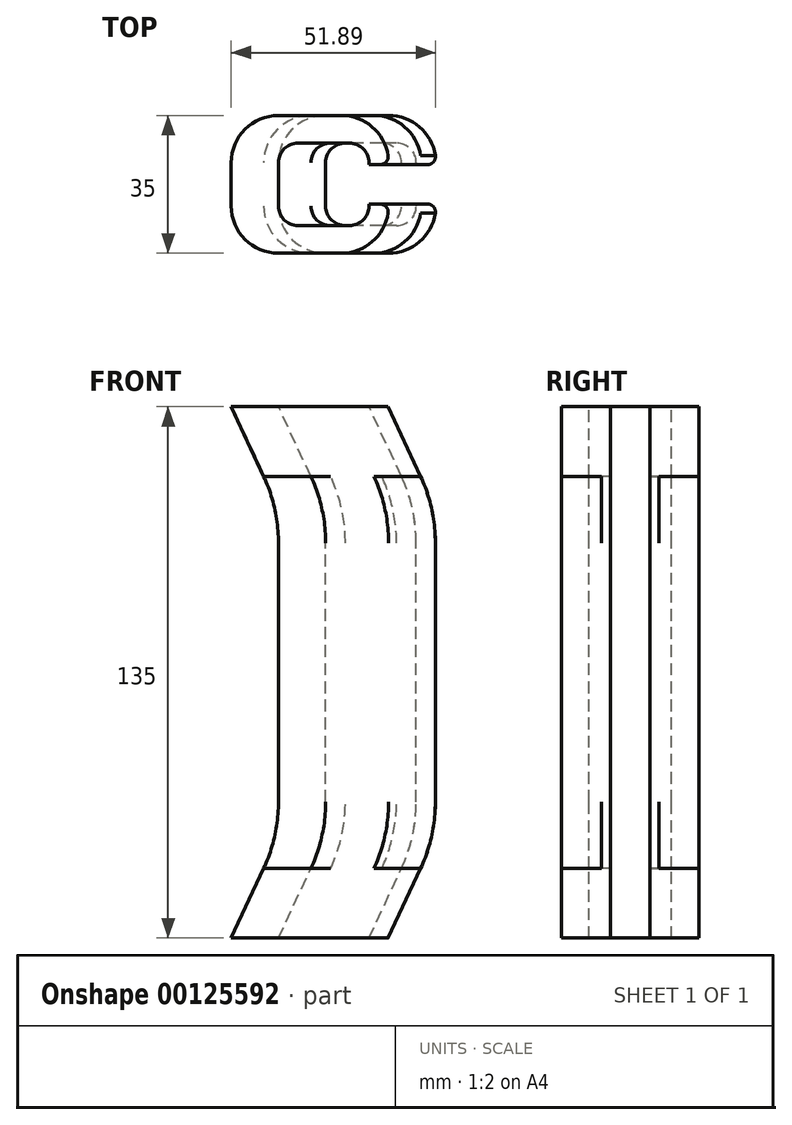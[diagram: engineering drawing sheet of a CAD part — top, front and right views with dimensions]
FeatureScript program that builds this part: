
annotation { "Feature Type Name" : "Feature", "Feature Type Description" : "" }
export const myFeature = defineFeature(function(context is Context, id is Id, definition is map)
    precondition{}
    {
        {
            var Q0;
            Q0=qCreatedBy(makeId("Top.planeOp"),FACE);
            var sketch = newSketch(context, id + "F0", { "sketchPlane" : qUnion([Q0])});
            skLineSegment(sketch, "E0.bottom", {"start": v(0, 17.5) * mm, "end": v(16, 17.5) * mm});
            skLineSegment(sketch, "E0.top", {"start": v(0, -17.5) * mm, "end": v(16, -17.5) * mm});
            skLineSegment(sketch, "E0.left", {"start": v(-12, 5.5) * mm, "end": v(-12, -5.5) * mm});
            skLineSegment(sketch, "E0.right", {"start": v(28, 5.5) * mm, "end": v(28, 5) * mm});
            skLineSegment(sketch, "E1.bottom", {"start": v(5, 10.5) * mm, "end": v(18, 10.5) * mm});
            skLineSegment(sketch, "E1.top", {"start": v(5, -10.5) * mm, "end": v(18, -10.5) * mm});
            skLineSegment(sketch, "E1.left", {"start": v(0, 5.5) * mm, "end": v(0, -5.5) * mm});
            skLineSegment(sketch, "E1.right", {"start": v(23, 5.5) * mm, "end": v(23, 5) * mm});
            skLineSegment(sketch, "E2.bottom", {"start": v(23, -5) * mm, "end": v(28, -5) * mm});
            skLineSegment(sketch, "E2.top", {"start": v(23, 5) * mm, "end": v(28, 5) * mm});
            skLineSegment(sketch, "E3.trimOffspring", {"start": v(23, -5) * mm, "end": v(23, -5.5) * mm});
            skLineSegment(sketch, "E4.trimOffspring", {"start": v(28, -5) * mm, "end": v(28, -5.5) * mm});
            skPoint(sketch, "E5.visualSharp", {"position": v(23, 10.5) * mm});
            skArc(sketch, "E5.filletArc", {"start": v(23, 5.5) * mm, "mid": v(21.54, 9.04) * mm, "end": v(18, 10.5) * mm});
            skPoint(sketch, "E6.visualSharp", {"position": v(23, -10.5) * mm});
            skArc(sketch, "E6.filletArc", {"start": v(18, -10.5) * mm, "mid": v(21.54, -9.04) * mm, "end": v(23, -5.5) * mm});
            skPoint(sketch, "E7.visualSharp", {"position": v(0, -10.5) * mm});
            skArc(sketch, "E7.filletArc", {"start": v(0, -5.5) * mm, "mid": v(1.46, -9.04) * mm, "end": v(5, -10.5) * mm});
            skPoint(sketch, "E8.visualSharp", {"position": v(0, 10.5) * mm});
            skArc(sketch, "E8.filletArc", {"start": v(5, 10.5) * mm, "mid": v(1.46, 9.04) * mm, "end": v(0, 5.5) * mm});
            skPoint(sketch, "E9.visualSharp", {"position": v(28, 17.5) * mm});
            skArc(sketch, "E9.filletArc", {"start": v(28, 5.5) * mm, "mid": v(24.49, 13.99) * mm, "end": v(16, 17.5) * mm});
            skPoint(sketch, "E10.visualSharp", {"position": v(28, -17.5) * mm});
            skArc(sketch, "E10.filletArc", {"start": v(16, -17.5) * mm, "mid": v(24.49, -13.99) * mm, "end": v(28, -5.5) * mm});
            skPoint(sketch, "E11.visualSharp", {"position": v(-12, -17.5) * mm});
            skArc(sketch, "E11.filletArc", {"start": v(-12, -5.5) * mm, "mid": v(-8.49, -13.99) * mm, "end": v(0, -17.5) * mm});
            skPoint(sketch, "E12.visualSharp", {"position": v(-12, 17.5) * mm});
            skArc(sketch, "E12.filletArc", {"start": v(0, 17.5) * mm, "mid": v(-8.49, 13.99) * mm, "end": v(-12, 5.5) * mm});
            skSolve(sketch);
        }
        {
            var Q0;
            Q0=qCreatedBy(makeId("Front.planeOp"),FACE);
            var sketch = newSketch(context, id + "F1", { "sketchPlane" : qUnion([Q0])});
            skLineSegment(sketch, "E13", {"start": v(-12, 0) * mm, "end": v(-3.75, 17.7) * mm});
            skLineSegment(sketch, "E14", {"start": v(0, 34.6) * mm, "end": v(0, 100.4) * mm});
            skLineSegment(sketch, "E15", {"start": v(-3.75, 117.3) * mm, "end": v(-12, 135) * mm});
            skPoint(sketch, "E16.visualSharp", {"position": v(0, 25.73) * mm});
            skArc(sketch, "E16.filletArc", {"start": v(-3.75, 17.7) * mm, "mid": v(-0.95, 25.94) * mm, "end": v(0, 34.6) * mm});
            skPoint(sketch, "E17.visualSharp", {"position": v(0, 109.27) * mm});
            skArc(sketch, "E17.filletArc", {"start": v(0, 100.4) * mm, "mid": v(-0.95, 109.06) * mm, "end": v(-3.75, 117.3) * mm});
            skSolve(sketch);
        }
        {
            var Q0;
            Q0=makeQuery(id+"F0.imprint","IMPRINT",FACE,{"disambiguationData":[TD([[makeQuery(id+"F0.imprint","IMPRINT",EDGE,{"derivedFrom":sQuery(id+"F0.wireOp",EDGE,"E0.bottom")}),-1.0]])]});
            var Q1;
            Q1=sQuery(id+"F1.wireOp",EDGE,"E13");
            var Q2;
            Q2=sQuery(id+"F1.wireOp",EDGE,"E16.filletArc");
            var Q3;
            Q3=sQuery(id+"F1.wireOp",EDGE,"E14");
            var Q4;
            Q4=sQuery(id+"F1.wireOp",EDGE,"E17.filletArc");
            var Q5;
            Q5=sQuery(id+"F1.wireOp",EDGE,"E15");
            sweep(context, id + "F2", {"profiles" : qUnion([Q0]), "path" : qUnion([Q1, Q2, Q3, Q4, Q5]), "keepProfileOrientation" : true});
        }
        {
            var Q0;
            Q0=makeQuery(id+"F2.opSweep","SWEPT_EDGE",EDGE,{"disambiguationData":[OSD([sQuery(id+"F0.wireOp",EDGE,"E2.bottom"),sQuery(id+"F0.wireOp",EDGE,"E4.trimOffspring"),sQuery(id+"F1.wireOp",EDGE,"E13")])]});
            var Q1;
            Q1=makeQuery(id+"F2.opSweep","SWEPT_EDGE",EDGE,{"disambiguationData":[OSD([sQuery(id+"F0.wireOp",EDGE,"E0.right"),sQuery(id+"F0.wireOp",EDGE,"E2.top"),sQuery(id+"F1.wireOp",EDGE,"E13")])]});
            fillet(context, id + "F3", {"entities" : qUnion([Q0, Q1]), "radius" : 2 * mm, "tangentPropagation" : true, "allowEdgeOverflow" : false});
        }
    });
